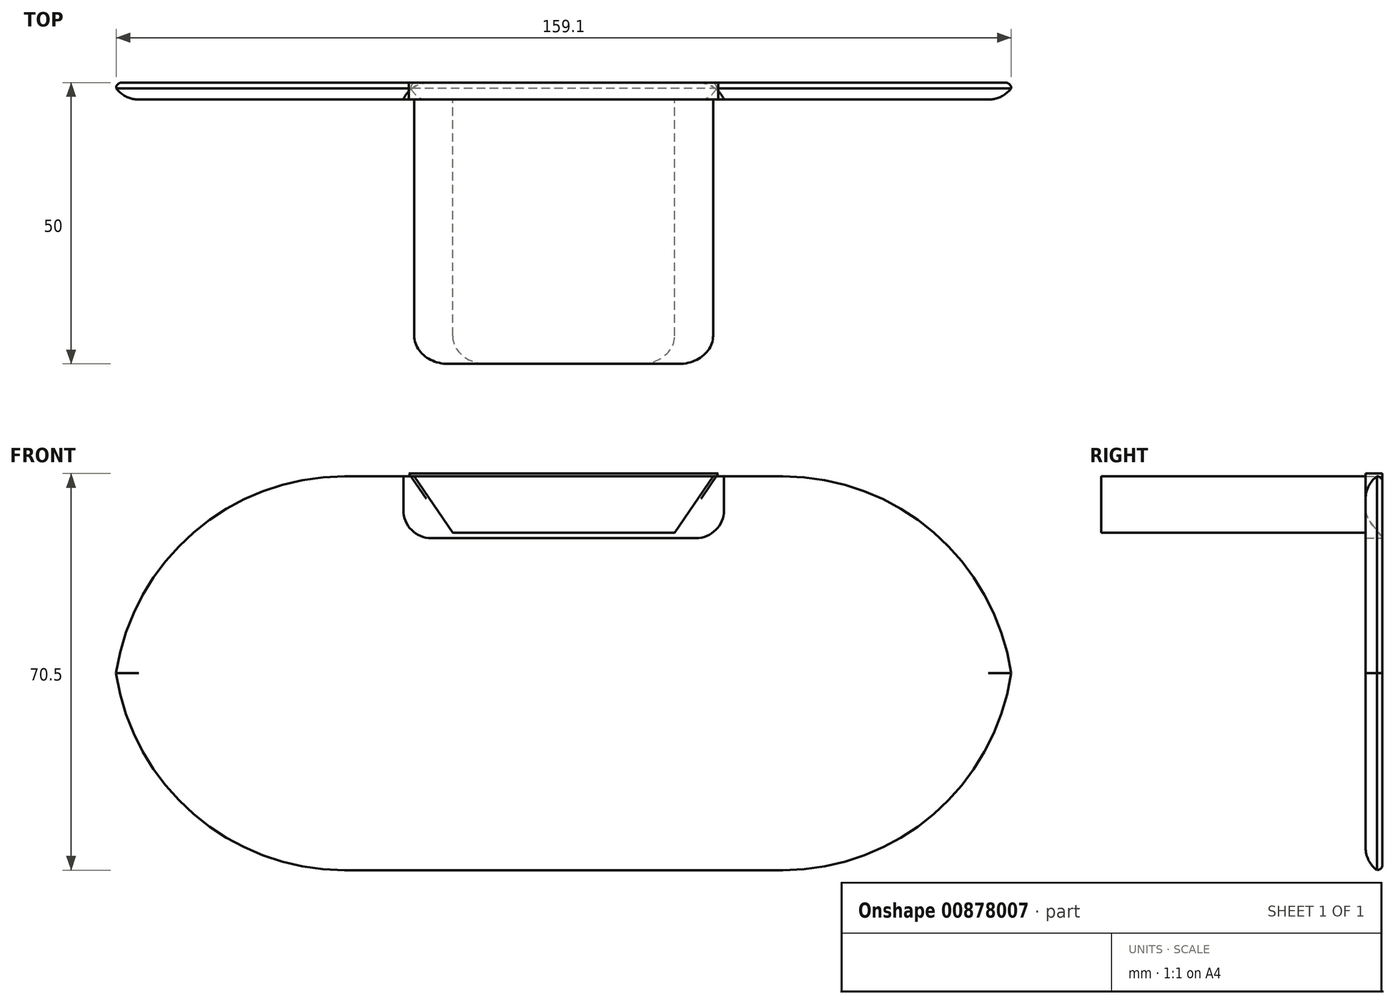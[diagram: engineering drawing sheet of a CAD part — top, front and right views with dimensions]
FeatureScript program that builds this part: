
annotation { "Feature Type Name" : "Feature", "Feature Type Description" : "" }
export const myFeature = defineFeature(function(context is Context, id is Id, definition is map)
    precondition{}
    {
        {
            var Q0;
            Q0=qCreatedBy(makeId("Front.planeOp"),FACE);
            var sketch = newSketch(context, id + "F0", { "sketchPlane" : qUnion([Q0])});
            skLineSegment(sketch, "E0.bottom", {"start": v(-20, -6.88) * mm, "end": v(20, -6.87) * mm});
            skLineSegment(sketch, "E1", {"start": v(27.5, 4.13) * mm, "end": v(20, -6.88) * mm});
            skLineSegment(sketch, "E2", {"start": v(-27.5, 4.12) * mm, "end": v(-20, -6.88) * mm});
            skLineSegment(sketch, "E3", {"start": v(-27.5, 4.12) * mm, "end": v(27.5, 4.13) * mm});
            skLineSegment(sketch, "E4.0", {"start": v(-27.5, 3.62) * mm, "end": v(27.5, 3.63) * mm});
            skLineSegment(sketch, "E5.0", {"start": v(-27.09, 4.4) * mm, "end": v(-19.59, -6.6) * mm});
            skLineSegment(sketch, "E6.0", {"start": v(-20, -6.38) * mm, "end": v(20, -6.37) * mm});
            skLineSegment(sketch, "E7.0", {"start": v(27.09, 4.4) * mm, "end": v(19.59, -6.6) * mm});
            skLineSegment(sketch, "E8.bottom", {"start": v(28.5, 3.63) * mm, "end": v(-28.5, 3.63) * mm});
            skLineSegment(sketch, "E8.top", {"start": v(28.5, -7.37) * mm, "end": v(-28.5, -7.38) * mm});
            skLineSegment(sketch, "E8.left", {"start": v(28.5, 3.63) * mm, "end": v(28.5, -7.37) * mm});
            skLineSegment(sketch, "E8.right", {"start": v(-28.5, 3.63) * mm, "end": v(-28.5, -7.38) * mm});
            skLineSegment(sketch, "E9.bottom", {"start": v(80, 3.62) * mm, "end": v(-80, 3.62) * mm});
            skLineSegment(sketch, "E9.top", {"start": v(80, -66.37) * mm, "end": v(-80, -66.38) * mm});
            skLineSegment(sketch, "E9.left", {"start": v(80, 3.63) * mm, "end": v(80, -66.37) * mm});
            skLineSegment(sketch, "E9.right", {"start": v(-80, 3.63) * mm, "end": v(-80, -66.37) * mm});
            skSolve(sketch);
        }
        {
            var Q0;
            {var subQ0=sQuery(id+"F0.wireOp",EDGE,"E5.0");var subQ1=sQuery(id+"F0.wireOp",EDGE,"E4.0");var subQ2=makeQuery(id+"F0.imprint","INTERSECT",VERTEX,{"derivedFrom":[subQ1,subQ0]});Q0=makeQuery(id+"F0.imprint","IMPRINT",FACE,{"disambiguationData":[TD([[makeQuery(id+"F0.imprint","IMPRINT",EDGE,{"disambiguationData":[TD([[subQ2,-1.0]])],"derivedFrom":subQ1}),-1.0]])]});}
            var Q1;
            {var subQ0=sQuery(id+"F0.wireOp",EDGE,"E6.0");var subQ1=sQuery(id+"F0.wireOp",EDGE,"E5.0");var subQ2=makeQuery(id+"F0.imprint","INTERSECT",VERTEX,{"derivedFrom":[subQ1,subQ0]});Q1=makeQuery(id+"F0.imprint","IMPRINT",FACE,{"disambiguationData":[TD([[makeQuery(id+"F0.imprint","IMPRINT",EDGE,{"disambiguationData":[TD([[subQ2,1.0]])],"derivedFrom":subQ1}),1.0]])]});}
            extrude(context, id + "F1", {"entities" : qUnion([Q0, Q1]), "depth" : 50 * mm, "offsetDistance" : 25 * mm});
        }
        {
            var Q0;
            {var subQ4=sQuery(id+"F0.wireOp",EDGE,"E0.bottom");Q0=makeQuery(id+"F0.imprint","IMPRINT",FACE,{"disambiguationData":[TD([[makeQuery(id+"F0.imprint","IMPRINT",EDGE,{"derivedFrom":subQ4}),-1.0]])]});}
            var Q1;
            {var subQ0=sQuery(id+"F0.wireOp",EDGE,"E6.0");var subQ1=sQuery(id+"F0.wireOp",EDGE,"E5.0");var subQ2=makeQuery(id+"F0.imprint","INTERSECT",VERTEX,{"derivedFrom":[subQ1,subQ0]});Q1=makeQuery(id+"F0.imprint","IMPRINT",FACE,{"disambiguationData":[TD([[makeQuery(id+"F0.imprint","IMPRINT",EDGE,{"disambiguationData":[TD([[subQ2,1.0]])],"derivedFrom":subQ1}),1.0]])]});}
            var Q2;
            {var subQ6=sQuery(id+"F0.wireOp",EDGE,"E0.bottom");Q2=makeQuery(id+"F0.imprint","IMPRINT",FACE,{"disambiguationData":[TD([[makeQuery(id+"F0.imprint","IMPRINT",EDGE,{"derivedFrom":subQ6}),1.0]])]});}
            extrude(context, id + "F2", {"entities" : qUnion([Q0, Q1, Q2]), "operationType" : NewBodyOperationType.ADD, "depth" : 3 * mm, "offsetDistance" : 25 * mm});
        }
        {
            var Q0;
            Q0=makeQuery(id+"F2.opExtrude","SWEPT_EDGE",EDGE,{"disambiguationData":[OSD([sQuery(id+"F0.wireOp",EDGE,"E8.top"),sQuery(id+"F0.wireOp",EDGE,"E8.left")])]});
            var Q1;
            Q1=makeQuery(id+"F2.opExtrude","SWEPT_EDGE",EDGE,{"disambiguationData":[OSD([sQuery(id+"F0.wireOp",EDGE,"E8.top"),sQuery(id+"F0.wireOp",EDGE,"E8.right")])]});
            var Q2;
            Q2=makeQuery(id+"F2.opExtrude","CAP_EDGE",EDGE,{"disambiguationData":[OSD([sQuery(id+"F0.wireOp",EDGE,"E8.left")])],"isStart":true});
            var Q3;
            Q3=makeQuery(id+"F2.opExtrude","CAP_EDGE",EDGE,{"disambiguationData":[OSD([sQuery(id+"F0.wireOp",EDGE,"E8.right")])],"isStart":true});
            fillet(context, id + "F3", {"entities" : qUnion([Q0, Q1, Q2, Q3]), "radius" : 5 * mm, "tangentPropagation" : true, "allowEdgeOverflow" : false});
        }
        {
            var Q0;
            Q0=makeQuery(id+"F1.opExtrude","CAP_EDGE",EDGE,{"disambiguationData":[OSD([sQuery(id+"F0.wireOp",EDGE,"E7.0")])],"isStart":false});
            var Q1;
            Q1=makeQuery(id+"F1.opExtrude","CAP_EDGE",EDGE,{"disambiguationData":[OSD([sQuery(id+"F0.wireOp",EDGE,"E5.0")])],"isStart":false});
            fillet(context, id + "F4", {"entities" : qUnion([Q0, Q1]), "radius" : 5 * mm, "tangentPropagation" : true, "allowEdgeOverflow" : false});
        }
        {
            var Q0;
            Q0 = qSketchRegion(id + "F0", true);
            var Q1;
            {var subQ0=sQuery(id+"F0.wireOp",EDGE,"E6.0");var subQ1=sQuery(id+"F0.wireOp",EDGE,"E5.0");var subQ2=makeQuery(id+"F0.imprint","INTERSECT",VERTEX,{"derivedFrom":[subQ1,subQ0]});Q1=makeQuery(id+"F0.imprint","IMPRINT",FACE,{"disambiguationData":[TD([[makeQuery(id+"F0.imprint","IMPRINT",EDGE,{"disambiguationData":[TD([[subQ2,1.0]])],"derivedFrom":subQ1}),1.0]])]});}
            extrude(context, id + "F5", {"entities" : qUnion([Q0, Q1]), "depth" : 3 * mm, "offsetDistance" : 25 * mm});
        }
        {
            var Q0;
            Q0=makeQuery(id+"F5.opExtrude","SWEPT_EDGE",EDGE,{"disambiguationData":[OSD([sQuery(id+"F0.wireOp",EDGE,"E9.top"),sQuery(id+"F0.wireOp",EDGE,"E9.right")])]});
            var Q1;
            Q1=makeQuery(id+"F5.opExtrude","SWEPT_EDGE",EDGE,{"disambiguationData":[OSD([sQuery(id+"F0.wireOp",EDGE,"E9.bottom"),sQuery(id+"F0.wireOp",EDGE,"E9.right")])]});
            var Q2;
            Q2=makeQuery(id+"F5.opExtrude","SWEPT_EDGE",EDGE,{"disambiguationData":[OSD([sQuery(id+"F0.wireOp",EDGE,"E9.bottom"),sQuery(id+"F0.wireOp",EDGE,"E9.left")])]});
            var Q3;
            Q3=makeQuery(id+"F5.opExtrude","SWEPT_EDGE",EDGE,{"disambiguationData":[OSD([sQuery(id+"F0.wireOp",EDGE,"E9.top"),sQuery(id+"F0.wireOp",EDGE,"E9.left")])]});
            fillet(context, id + "F6", {"entities" : qUnion([Q0, Q1, Q2, Q3]), "radius" : 41.04 * mm, "tangentPropagation" : true, "allowEdgeOverflow" : false});
        }
        {
            var Q0;
            {var subQ0=sQuery(id+"F0.wireOp",EDGE,"E9.left");var subQ1=sQuery(id+"F0.wireOp",EDGE,"E9.bottom");Q0=makeQuery(id+"F6.opFillet","BLEND_EDGE",EDGE,{"blendedFrom":[makeQuery(id+"F5.opExtrude","SWEPT_EDGE",EDGE,{"disambiguationData":[OSD([subQ1,subQ0])]}),makeQuery(id+"F5.opExtrude","CAP_FACE",FACE,{"disambiguationData":[OSD([sQuery(id+"F0.wireOp",EDGE,"E1"),sQuery(id+"F0.wireOp",EDGE,"E2"),sQuery(id+"F0.wireOp",EDGE,"E3"),sQuery(id+"F0.wireOp",EDGE,"E5.0"),sQuery(id+"F0.wireOp",EDGE,"E6.0"),sQuery(id+"F0.wireOp",EDGE,"E7.0"),subQ1,sQuery(id+"F0.wireOp",EDGE,"E9.top"),subQ0,sQuery(id+"F0.wireOp",EDGE,"E9.right")])],"isStart":true})],"blendedInto":[makeQuery(id+"F5.opExtrude","CAP_FACE",FACE,{"disambiguationData":[OSD([sQuery(id+"F0.wireOp",EDGE,"E1"),sQuery(id+"F0.wireOp",EDGE,"E2"),sQuery(id+"F0.wireOp",EDGE,"E3"),sQuery(id+"F0.wireOp",EDGE,"E5.0"),sQuery(id+"F0.wireOp",EDGE,"E6.0"),sQuery(id+"F0.wireOp",EDGE,"E7.0"),subQ1,sQuery(id+"F0.wireOp",EDGE,"E9.top"),subQ0,sQuery(id+"F0.wireOp",EDGE,"E9.right")])],"isStart":true})]});}
            var Q1;
            {var subQ0=sQuery(id+"F0.wireOp",EDGE,"E9.left");var subQ1=sQuery(id+"F0.wireOp",EDGE,"E9.top");Q1=makeQuery(id+"F6.opFillet","BLEND_EDGE",EDGE,{"blendedFrom":[makeQuery(id+"F5.opExtrude","SWEPT_EDGE",EDGE,{"disambiguationData":[OSD([subQ1,subQ0])]}),makeQuery(id+"F5.opExtrude","CAP_FACE",FACE,{"disambiguationData":[OSD([sQuery(id+"F0.wireOp",EDGE,"E1"),sQuery(id+"F0.wireOp",EDGE,"E2"),sQuery(id+"F0.wireOp",EDGE,"E3"),sQuery(id+"F0.wireOp",EDGE,"E5.0"),sQuery(id+"F0.wireOp",EDGE,"E6.0"),sQuery(id+"F0.wireOp",EDGE,"E7.0"),sQuery(id+"F0.wireOp",EDGE,"E9.bottom"),subQ1,subQ0,sQuery(id+"F0.wireOp",EDGE,"E9.right")])],"isStart":true})],"blendedInto":[makeQuery(id+"F5.opExtrude","CAP_FACE",FACE,{"disambiguationData":[OSD([sQuery(id+"F0.wireOp",EDGE,"E1"),sQuery(id+"F0.wireOp",EDGE,"E2"),sQuery(id+"F0.wireOp",EDGE,"E3"),sQuery(id+"F0.wireOp",EDGE,"E5.0"),sQuery(id+"F0.wireOp",EDGE,"E6.0"),sQuery(id+"F0.wireOp",EDGE,"E7.0"),sQuery(id+"F0.wireOp",EDGE,"E9.bottom"),subQ1,subQ0,sQuery(id+"F0.wireOp",EDGE,"E9.right")])],"isStart":true})]});}
            var Q2;
            {var subQ0=sQuery(id+"F0.wireOp",EDGE,"E9.right");var subQ1=sQuery(id+"F0.wireOp",EDGE,"E9.bottom");Q2=makeQuery(id+"F6.opFillet","BLEND_EDGE",EDGE,{"blendedFrom":[makeQuery(id+"F5.opExtrude","SWEPT_EDGE",EDGE,{"disambiguationData":[OSD([subQ1,subQ0])]}),makeQuery(id+"F5.opExtrude","CAP_FACE",FACE,{"disambiguationData":[OSD([sQuery(id+"F0.wireOp",EDGE,"E1"),sQuery(id+"F0.wireOp",EDGE,"E2"),sQuery(id+"F0.wireOp",EDGE,"E3"),sQuery(id+"F0.wireOp",EDGE,"E5.0"),sQuery(id+"F0.wireOp",EDGE,"E6.0"),sQuery(id+"F0.wireOp",EDGE,"E7.0"),subQ1,sQuery(id+"F0.wireOp",EDGE,"E9.top"),sQuery(id+"F0.wireOp",EDGE,"E9.left"),subQ0])],"isStart":true})],"blendedInto":[makeQuery(id+"F5.opExtrude","CAP_FACE",FACE,{"disambiguationData":[OSD([sQuery(id+"F0.wireOp",EDGE,"E1"),sQuery(id+"F0.wireOp",EDGE,"E2"),sQuery(id+"F0.wireOp",EDGE,"E3"),sQuery(id+"F0.wireOp",EDGE,"E5.0"),sQuery(id+"F0.wireOp",EDGE,"E6.0"),sQuery(id+"F0.wireOp",EDGE,"E7.0"),subQ1,sQuery(id+"F0.wireOp",EDGE,"E9.top"),sQuery(id+"F0.wireOp",EDGE,"E9.left"),subQ0])],"isStart":true})]});}
            fillet(context, id + "F7", {"entities" : qUnion([Q0, Q1, Q2]), "radius" : 1 * mm, "tangentPropagation" : true, "allowEdgeOverflow" : false});
        }
        {
            var Q0;
            {var subQ0=sQuery(id+"F0.wireOp",EDGE,"E9.right");var subQ1=sQuery(id+"F0.wireOp",EDGE,"E9.top");Q0=makeQuery(id+"F6.opFillet","BLEND_EDGE",EDGE,{"blendedFrom":[makeQuery(id+"F5.opExtrude","SWEPT_EDGE",EDGE,{"disambiguationData":[OSD([subQ1,subQ0])]}),makeQuery(id+"F5.opExtrude","CAP_FACE",FACE,{"disambiguationData":[OSD([sQuery(id+"F0.wireOp",EDGE,"E1"),sQuery(id+"F0.wireOp",EDGE,"E2"),sQuery(id+"F0.wireOp",EDGE,"E3"),sQuery(id+"F0.wireOp",EDGE,"E5.0"),sQuery(id+"F0.wireOp",EDGE,"E6.0"),sQuery(id+"F0.wireOp",EDGE,"E7.0"),sQuery(id+"F0.wireOp",EDGE,"E9.bottom"),subQ1,sQuery(id+"F0.wireOp",EDGE,"E9.left"),subQ0])],"isStart":false})],"blendedInto":[makeQuery(id+"F5.opExtrude","CAP_FACE",FACE,{"disambiguationData":[OSD([sQuery(id+"F0.wireOp",EDGE,"E1"),sQuery(id+"F0.wireOp",EDGE,"E2"),sQuery(id+"F0.wireOp",EDGE,"E3"),sQuery(id+"F0.wireOp",EDGE,"E5.0"),sQuery(id+"F0.wireOp",EDGE,"E6.0"),sQuery(id+"F0.wireOp",EDGE,"E7.0"),sQuery(id+"F0.wireOp",EDGE,"E9.bottom"),subQ1,sQuery(id+"F0.wireOp",EDGE,"E9.left"),subQ0])],"isStart":false})]});}
            var Q1;
            {var subQ0=sQuery(id+"F0.wireOp",EDGE,"E9.right");var subQ1=sQuery(id+"F0.wireOp",EDGE,"E9.bottom");Q1=makeQuery(id+"F6.opFillet","BLEND_EDGE",EDGE,{"blendedFrom":[makeQuery(id+"F5.opExtrude","SWEPT_EDGE",EDGE,{"disambiguationData":[OSD([subQ1,subQ0])]}),makeQuery(id+"F5.opExtrude","CAP_FACE",FACE,{"disambiguationData":[OSD([sQuery(id+"F0.wireOp",EDGE,"E1"),sQuery(id+"F0.wireOp",EDGE,"E2"),sQuery(id+"F0.wireOp",EDGE,"E3"),sQuery(id+"F0.wireOp",EDGE,"E5.0"),sQuery(id+"F0.wireOp",EDGE,"E6.0"),sQuery(id+"F0.wireOp",EDGE,"E7.0"),subQ1,sQuery(id+"F0.wireOp",EDGE,"E9.top"),sQuery(id+"F0.wireOp",EDGE,"E9.left"),subQ0])],"isStart":false})],"blendedInto":[makeQuery(id+"F5.opExtrude","CAP_FACE",FACE,{"disambiguationData":[OSD([sQuery(id+"F0.wireOp",EDGE,"E1"),sQuery(id+"F0.wireOp",EDGE,"E2"),sQuery(id+"F0.wireOp",EDGE,"E3"),sQuery(id+"F0.wireOp",EDGE,"E5.0"),sQuery(id+"F0.wireOp",EDGE,"E6.0"),sQuery(id+"F0.wireOp",EDGE,"E7.0"),subQ1,sQuery(id+"F0.wireOp",EDGE,"E9.top"),sQuery(id+"F0.wireOp",EDGE,"E9.left"),subQ0])],"isStart":false})]});}
            var Q2;
            {var subQ0=sQuery(id+"F0.wireOp",EDGE,"E9.left");var subQ1=sQuery(id+"F0.wireOp",EDGE,"E9.bottom");Q2=makeQuery(id+"F6.opFillet","BLEND_EDGE",EDGE,{"blendedFrom":[makeQuery(id+"F5.opExtrude","SWEPT_EDGE",EDGE,{"disambiguationData":[OSD([subQ1,subQ0])]}),makeQuery(id+"F5.opExtrude","CAP_FACE",FACE,{"disambiguationData":[OSD([sQuery(id+"F0.wireOp",EDGE,"E1"),sQuery(id+"F0.wireOp",EDGE,"E2"),sQuery(id+"F0.wireOp",EDGE,"E3"),sQuery(id+"F0.wireOp",EDGE,"E5.0"),sQuery(id+"F0.wireOp",EDGE,"E6.0"),sQuery(id+"F0.wireOp",EDGE,"E7.0"),subQ1,sQuery(id+"F0.wireOp",EDGE,"E9.top"),subQ0,sQuery(id+"F0.wireOp",EDGE,"E9.right")])],"isStart":false})],"blendedInto":[makeQuery(id+"F5.opExtrude","CAP_FACE",FACE,{"disambiguationData":[OSD([sQuery(id+"F0.wireOp",EDGE,"E1"),sQuery(id+"F0.wireOp",EDGE,"E2"),sQuery(id+"F0.wireOp",EDGE,"E3"),sQuery(id+"F0.wireOp",EDGE,"E5.0"),sQuery(id+"F0.wireOp",EDGE,"E6.0"),sQuery(id+"F0.wireOp",EDGE,"E7.0"),subQ1,sQuery(id+"F0.wireOp",EDGE,"E9.top"),subQ0,sQuery(id+"F0.wireOp",EDGE,"E9.right")])],"isStart":false})]});}
            fillet(context, id + "F8", {"entities" : qUnion([Q0, Q1, Q2]), "radius" : 5 * mm, "tangentPropagation" : true, "allowEdgeOverflow" : false});
        }
    });
